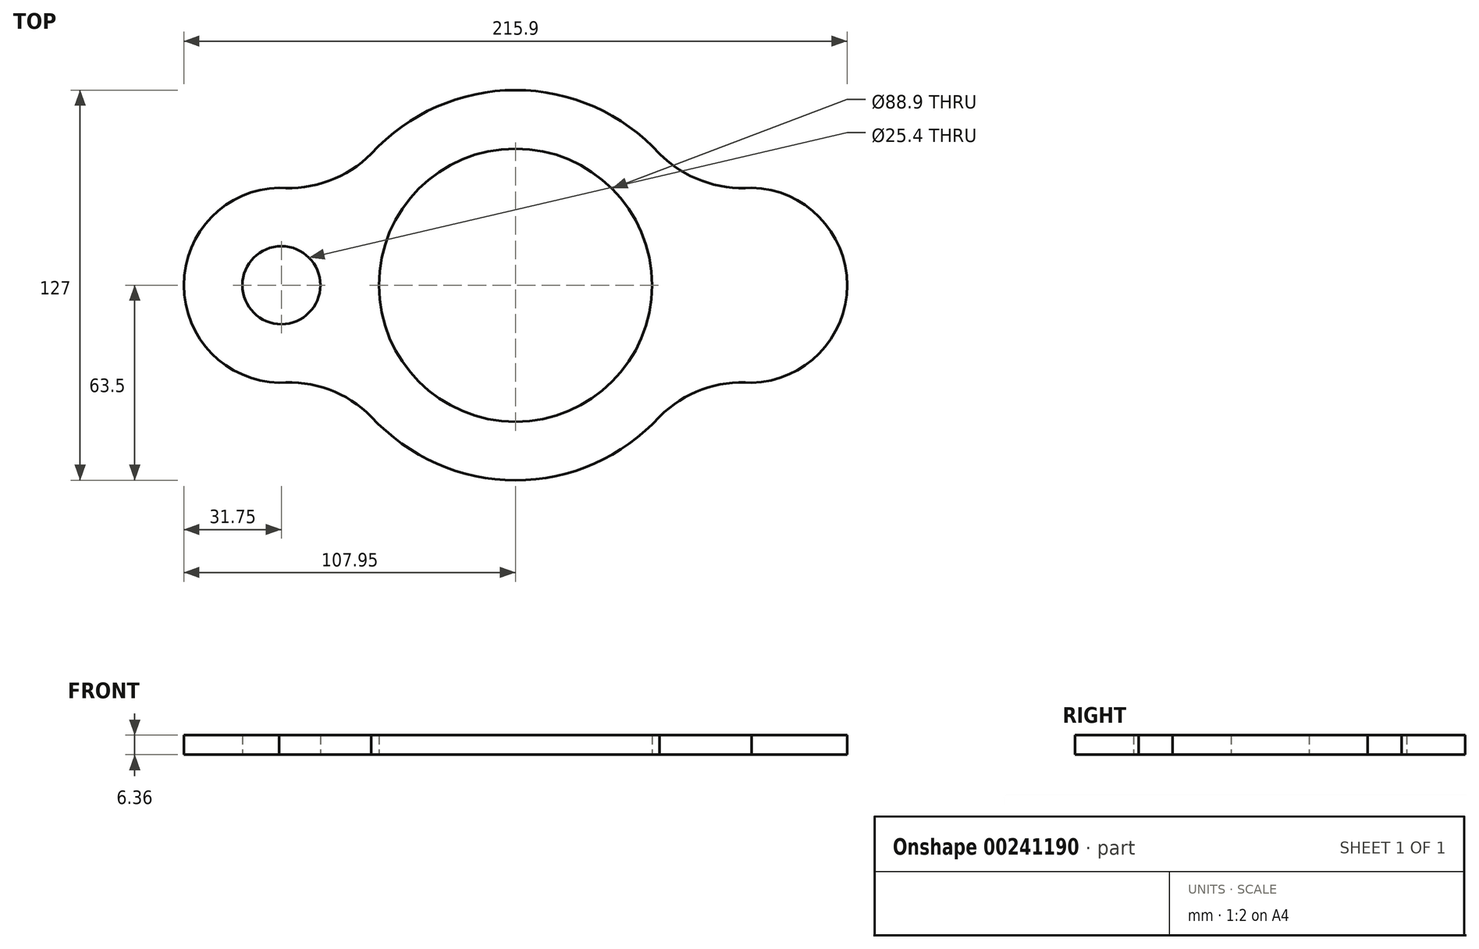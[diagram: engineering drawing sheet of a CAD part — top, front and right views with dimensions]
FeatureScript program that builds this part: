
annotation { "Feature Type Name" : "Feature", "Feature Type Description" : "" }
export const myFeature = defineFeature(function(context is Context, id is Id, definition is map)
    precondition{}
    {
        {
            var Q0;
            Q0=qCreatedBy(makeId("Top.planeOp"),FACE);
            var sketch = newSketch(context, id + "F0", { "sketchPlane" : qUnion([Q0])});
            skCircle(sketch, "E0", {"center": v(0, 0) * mm, "radius": 44.45 * mm});
            skCircle(sketch, "E1", {"center": v(-76.2, 0) * mm, "radius": 12.7 * mm});
            skCircle(sketch, "E2.MirrorC", {"center": v(76.2, 0) * mm, "radius": 12.7 * mm});
            skArc(sketch, "E3", {"start": v(73.39, -31.62) * mm, "mid": v(107.95, 0) * mm, "end": v(73.39, 31.62) * mm});
            skArc(sketch, "E4", {"start": v(-76.9, 31.74) * mm, "mid": v(-60.7, 33.97) * mm, "end": v(-46.93, 42.77) * mm});
            skArc(sketch, "E5.MirrorCS", {"start": v(76.9, 31.74) * mm, "mid": v(60.7, 33.97) * mm, "end": v(46.93, 42.77) * mm});
            skArc(sketch, "E6.MirrorCS", {"start": v(-76.9, -31.74) * mm, "mid": v(-60.7, -33.97) * mm, "end": v(-46.93, -42.77) * mm});
            skArc(sketch, "E7.MirrorCS", {"start": v(76.9, -31.74) * mm, "mid": v(60.7, -33.97) * mm, "end": v(46.93, -42.77) * mm});
            skArc(sketch, "E8.trimOffspring", {"start": v(-76.9, -31.74) * mm, "mid": v(-107.95, 0) * mm, "end": v(-76.9, 31.74) * mm});
            skArc(sketch, "E9.trimOffspring", {"start": v(-46.93, -42.77) * mm, "mid": v(0, -63.5) * mm, "end": v(46.93, -42.77) * mm});
            skArc(sketch, "E10.trimOffspring", {"start": v(46.93, 42.77) * mm, "mid": v(0, 63.5) * mm, "end": v(-46.93, 42.77) * mm});
            skSolve(sketch);
        }
        {
            var Q0;
            {var subQ0=sQuery(id+"F0.wireOp",EDGE,"E1");Q0=makeQuery(id+"F0.imprint","IMPRINT",FACE,{"disambiguationData":[TD([[makeQuery(id+"F0.imprint","IMPRINT",EDGE,{"derivedFrom":subQ0}),-1.0]])]});}
            var Q1;
            {var subQ0=sQuery(id+"F0.wireOp",EDGE,"E4");var subQ1=sQuery(id+"F0.wireOp",EDGE,"JGrXhBAY-uZfW-qp34-4ziJ-5hWKh1Bzp4wD");var subQ2=makeQuery(id+"F0.imprint","INTERSECT",VERTEX,{"derivedFrom":[subQ1,subQ0]});Q1=makeQuery(id+"F0.imprint","IMPRINT",FACE,{"disambiguationData":[TD([[makeQuery(id+"F0.imprint","IMPRINT",EDGE,{"disambiguationData":[TD([[subQ2,-1.0]])],"derivedFrom":subQ1}),-1.0]])]});}
            var Q2;
            {var subQ0=sQuery(id+"F0.wireOp",EDGE,"E6.MirrorCS");var subQ1=sQuery(id+"F0.wireOp",EDGE,"JGrXhBAY-uZfW-qp34-4ziJ-5hWKh1Bzp4wD");var subQ2=makeQuery(id+"F0.imprint","INTERSECT",VERTEX,{"derivedFrom":[subQ1,subQ0]});Q2=makeQuery(id+"F0.imprint","IMPRINT",FACE,{"disambiguationData":[TD([[makeQuery(id+"F0.imprint","IMPRINT",EDGE,{"disambiguationData":[TD([[subQ2,1.0]])],"derivedFrom":subQ1}),-1.0]])]});}
            var Q3;
            {var subQ2=sQuery(id+"F0.wireOp",EDGE,"E3");var subQ7=sQuery(id+"F0.wireOp",EDGE,"E0");var subQ8=makeQuery(id+"F0.imprint","INTERSECT",VERTEX,{"derivedFrom":[subQ7,subQ2]});Q3=makeQuery(id+"F0.imprint","IMPRINT",FACE,{"disambiguationData":[TD([[makeQuery(id+"F0.imprint","IMPRINT",EDGE,{"disambiguationData":[TD([[subQ8,1.0]])],"derivedFrom":subQ7}),-1.0]])]});}
            var Q4;
            {var subQ0=sQuery(id+"F0.wireOp",EDGE,"JGrXhBAY-uZfW-qp34-4ziJ-5hWKh1Bzp4wD");var subQ1=makeQuery(id+"F0.imprint","INTERSECT",VERTEX,{"derivedFrom":[subQ0,sQuery(id+"F0.wireOp",EDGE,"E1")]});Q4=makeQuery(id+"F0.imprint","IMPRINT",FACE,{"disambiguationData":[TD([[makeQuery(id+"F0.imprint","IMPRINT",EDGE,{"disambiguationData":[TD([[subQ1,1.0]])],"derivedFrom":subQ0}),1.0]])]});}
            var Q5;
            {var subQ4=sQuery(id+"F0.wireOp",EDGE,"E3");var subQ5=sQuery(id+"F0.wireOp",EDGE,"E0");var subQ6=makeQuery(id+"F0.imprint","INTERSECT",VERTEX,{"derivedFrom":[subQ5,subQ4]});Q5=makeQuery(id+"F0.imprint","IMPRINT",FACE,{"disambiguationData":[TD([[makeQuery(id+"F0.imprint","IMPRINT",EDGE,{"disambiguationData":[TD([[subQ6,-1.0]])],"derivedFrom":subQ5}),-1.0]])]});}
            var Q6;
            {var subQ0=sQuery(id+"F0.wireOp",EDGE,"JGrXhBAY-uZfW-qp34-4ziJ-5hWKh1Bzp4wD");var subQ1=makeQuery(id+"F0.imprint","INTERSECT",VERTEX,{"derivedFrom":[subQ0,sQuery(id+"F0.wireOp",EDGE,"E2.MirrorC")]});Q6=makeQuery(id+"F0.imprint","IMPRINT",FACE,{"disambiguationData":[TD([[makeQuery(id+"F0.imprint","IMPRINT",EDGE,{"disambiguationData":[TD([[subQ1,-1.0]])],"derivedFrom":subQ0}),1.0]])]});}
            var Q7;
            {var subQ5=sQuery(id+"F0.wireOp",EDGE,"E2.MirrorC");Q7=makeQuery(id+"F0.imprint","IMPRINT",FACE,{"disambiguationData":[TD([[makeQuery(id+"F0.imprint","IMPRINT",EDGE,{"derivedFrom":subQ5}),1.0]])]});}
            var Q8;
            {var subQ0=sQuery(id+"F0.wireOp",EDGE,"E5.MirrorCS");var subQ1=sQuery(id+"F0.wireOp",EDGE,"JGrXhBAY-uZfW-qp34-4ziJ-5hWKh1Bzp4wD");var subQ2=makeQuery(id+"F0.imprint","INTERSECT",VERTEX,{"derivedFrom":[subQ1,subQ0]});Q8=makeQuery(id+"F0.imprint","IMPRINT",FACE,{"disambiguationData":[TD([[makeQuery(id+"F0.imprint","IMPRINT",EDGE,{"disambiguationData":[TD([[subQ2,1.0]])],"derivedFrom":subQ1}),-1.0]])]});}
            var Q9;
            {var subQ0=sQuery(id+"F0.wireOp",EDGE,"E7.MirrorCS");var subQ1=sQuery(id+"F0.wireOp",EDGE,"JGrXhBAY-uZfW-qp34-4ziJ-5hWKh1Bzp4wD");var subQ2=makeQuery(id+"F0.imprint","INTERSECT",VERTEX,{"derivedFrom":[subQ1,subQ0]});Q9=makeQuery(id+"F0.imprint","IMPRINT",FACE,{"disambiguationData":[TD([[makeQuery(id+"F0.imprint","IMPRINT",EDGE,{"disambiguationData":[TD([[subQ2,-1.0]])],"derivedFrom":subQ1}),-1.0]])]});}
            extrude(context, id + "F1", {"entities" : qUnion([Q0, Q1, Q2, Q3, Q4, Q5, Q6, Q7, Q8, Q9]), "endBound" : BoundingType.SYMMETRIC, "depth" : 6.35 * mm});
        }
    });
